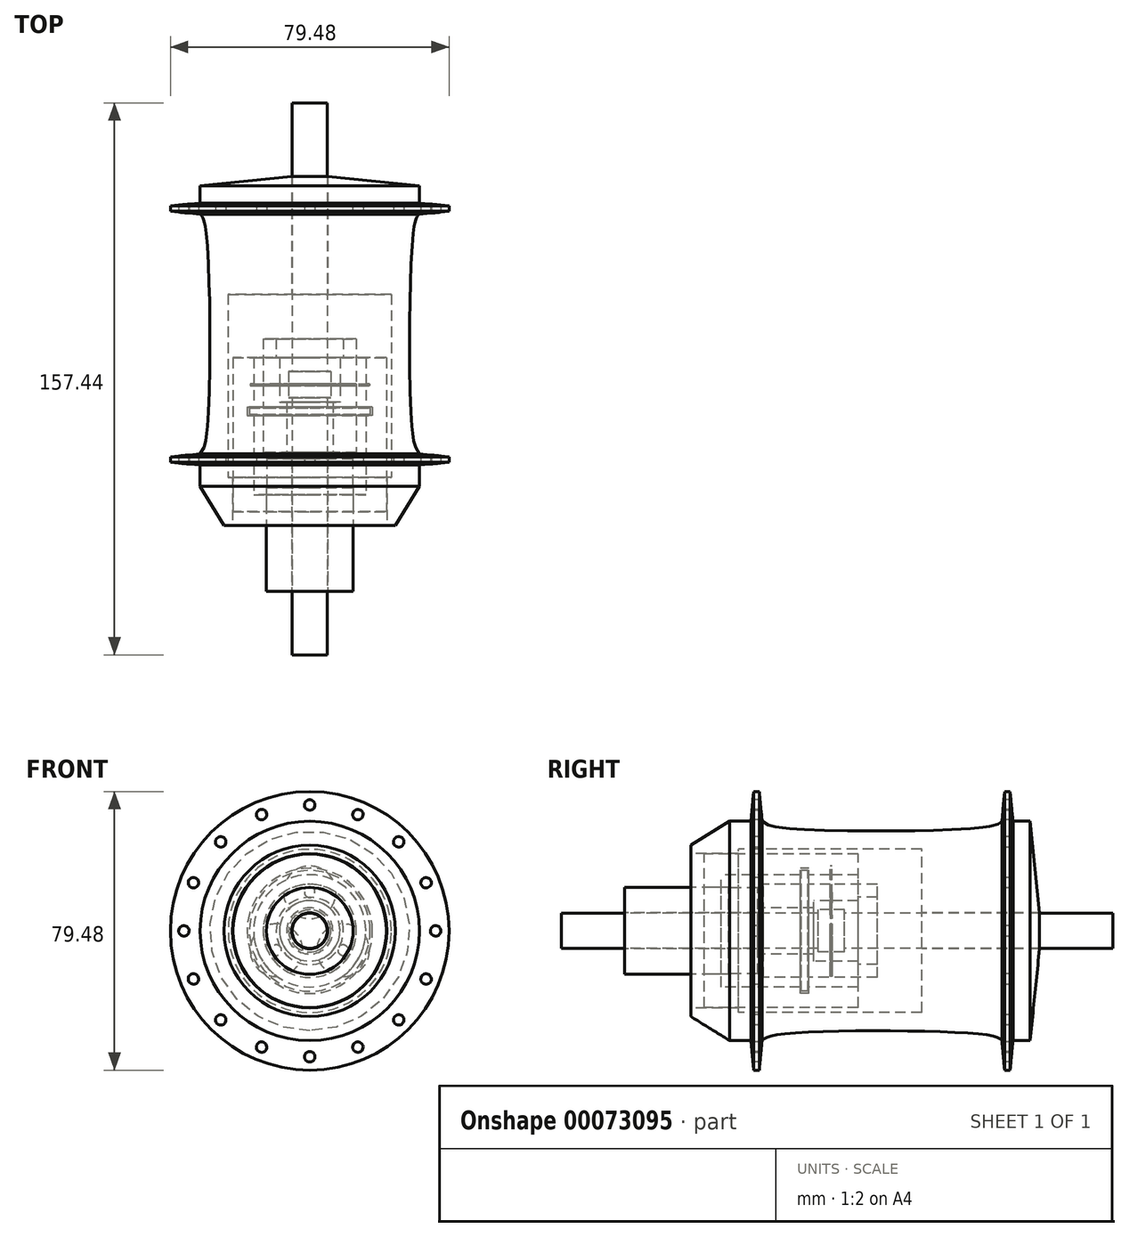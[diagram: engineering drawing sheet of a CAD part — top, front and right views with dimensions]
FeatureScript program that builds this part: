
annotation { "Feature Type Name" : "Feature", "Feature Type Description" : "" }
export const myFeature = defineFeature(function(context is Context, id is Id, definition is map)
    precondition{}
    {
        {
            assignVariable(context, id + "F0", {"name" : "gearWidth", "anyValue" : .5});
        }
        {
            var Q0;
            Q0=qCreatedBy(makeId("Right.planeOp"),FACE);
            var sketch = newSketch(context, id + "F1", { "sketchPlane" : qUnion([Q0])});
            skLineSegment(sketch, "E0", {"start": v(-26.68, 31.27) * mm, "end": v(-20.6, 31.27) * mm});
            skLineSegment(sketch, "E1", {"start": v(59.06, 31.27) * mm, "end": v(61.75, 5.13) * mm});
            skLineSegment(sketch, "E2", {"start": v(61.75, 5.13) * mm, "end": v(28.14, 5.13) * mm});
            skLineSegment(sketch, "E3", {"start": v(28.14, 5.13) * mm, "end": v(28.14, 23.27) * mm});
            skLineSegment(sketch, "E4", {"start": v(28.14, 23.27) * mm, "end": v(-24.12, 23.27) * mm});
            skLineSegment(sketch, "E5", {"start": v(-37.77, 24.44) * mm, "end": v(-26.68, 31.27) * mm});
            skLineSegment(sketch, "E6", {"start": v(-20.6, 31.27) * mm, "end": v(-19.8, 39.74) * mm});
            skLineSegment(sketch, "E7", {"start": v(-19.8, 39.74) * mm, "end": v(-18.22, 39.74) * mm});
            skLineSegment(sketch, "E8", {"start": v(-18.22, 39.74) * mm, "end": v(-17.43, 31.27) * mm});
            skLineSegment(sketch, "E9", {"start": v(50.99, 31.27) * mm, "end": v(51.78, 39.74) * mm});
            skLineSegment(sketch, "E10", {"start": v(51.78, 39.74) * mm, "end": v(53.37, 39.74) * mm});
            skLineSegment(sketch, "E11", {"start": v(53.37, 39.74) * mm, "end": v(54.16, 31.27) * mm});
            skLineSegment(sketch, "E12.trimOffspring", {"start": v(54.16, 31.27) * mm, "end": v(59.06, 31.27) * mm});
            skLineSegment(sketch, "E13", {"start": v(-67.5, 0) * mm, "end": v(67.5, 0) * mm, "construction": true});
            skFitSpline(sketch, "E14", {"points": [v(-17.43, 31.27) * mm, v(-13, 29.59) * mm, v(46.1, 29.59) * mm, v(50.99, 31.27) * mm], "startDerivative": vector(15.28, -10.7) * mm, "endDerivative": vector(11.9, 12.75) * mm});
            skLineSegment(sketch, "E15", {"start": v(-33.92, 21.88) * mm, "end": v(10.01, 21.88) * mm});
            skLineSegment(sketch, "E16.bottom", {"start": v(-74.74, 5) * mm, "end": v(-1.42, 5) * mm});
            skLineSegment(sketch, "E16.top", {"start": v(-74.74, 0) * mm, "end": v(82.7, 0) * mm});
            skLineSegment(sketch, "E16.left", {"start": v(-74.74, 5) * mm, "end": v(-74.74, 0) * mm});
            skLineSegment(sketch, "E16.right", {"start": v(82.7, 5) * mm, "end": v(82.7, 0) * mm});
            skLineSegment(sketch, "E17.bottom", {"start": v(-56.63, 12.38) * mm, "end": v(-26.97, 12.38) * mm});
            skLineSegment(sketch, "E17.top", {"start": v(-56.63, 5.13) * mm, "end": v(-18.73, 5.13) * mm});
            skLineSegment(sketch, "E17.left", {"start": v(-56.63, 12.38) * mm, "end": v(-56.63, 5.13) * mm});
            skLineSegment(sketch, "E17.right", {"start": v(-18.73, 12.38) * mm, "end": v(-18.73, 5.13) * mm});
            skLineSegment(sketch, "E18.top", {"start": v(-18.73, 12.27) * mm, "end": v(-26.97, 12.27) * mm});
            skLineSegment(sketch, "E18.left", {"start": v(-18.73, 12.27) * mm, "end": v(-18.73, 12.38) * mm});
            skLineSegment(sketch, "E18.right", {"start": v(-26.97, 12.27) * mm, "end": v(-26.97, 12.38) * mm});
            skLineSegment(sketch, "E19", {"start": v(-33.92, 21.88) * mm, "end": v(-33.92, 16) * mm});
            skLineSegment(sketch, "E20", {"start": v(-29.03, 16) * mm, "end": v(-6.49, 16) * mm});
            skLineSegment(sketch, "E21", {"start": v(10.01, 16) * mm, "end": v(10.01, 21.88) * mm});
            skLineSegment(sketch, "E22.top", {"start": v(-37.77, 22.01) * mm, "end": v(-24.12, 22.01) * mm});
            skLineSegment(sketch, "E22.left", {"start": v(-37.77, 24.44) * mm, "end": v(-37.77, 22.01) * mm});
            skLineSegment(sketch, "E22.right", {"start": v(-24.12, 23.27) * mm, "end": v(-24.12, 22.01) * mm});
            skLineSegment(sketch, "E23.top", {"start": v(-33.92, 12.4) * mm, "end": v(-29.03, 12.4) * mm});
            skLineSegment(sketch, "E23.left", {"start": v(-33.92, 16) * mm, "end": v(-33.92, 12.4) * mm});
            skLineSegment(sketch, "E23.right", {"start": v(-29.03, 16) * mm, "end": v(-29.03, 12.4) * mm});
            skLineSegment(sketch, "E24.bottom", {"start": v(-17.02, 13.28) * mm, "end": v(-6.23, 13.28) * mm});
            skLineSegment(sketch, "E24.top", {"start": v(-17.02, 6.6) * mm, "end": v(-2.69, 6.6) * mm});
            skLineSegment(sketch, "E24.left", {"start": v(-17.02, 13.28) * mm, "end": v(-17.02, 6.6) * mm});
            skLineSegment(sketch, "E24.right", {"start": v(-2.69, 8.63) * mm, "end": v(-2.69, 6.6) * mm});
            skLineSegment(sketch, "E25.left", {"start": v(-6.49, 16) * mm, "end": v(-6.49, 17.88) * mm});
            skLineSegment(sketch, "E25.right", {"start": v(-4.03, 16) * mm, "end": v(-4.03, 17.88) * mm});
            skLineSegment(sketch, "E26.trimOffspring", {"start": v(-4.03, 16) * mm, "end": v(10.01, 16) * mm});
            skLineSegment(sketch, "E27", {"start": v(-4.03, 17.88) * mm, "end": v(-6.49, 17.88) * mm});
            skLineSegment(sketch, "E28.top", {"start": v(-6.23, 17.23) * mm, "end": v(-4.29, 17.23) * mm});
            skLineSegment(sketch, "E28.left", {"start": v(-6.23, 13.28) * mm, "end": v(-6.23, 17.23) * mm});
            skLineSegment(sketch, "E28.right", {"start": v(-4.29, 13.28) * mm, "end": v(-4.29, 17.23) * mm});
            skLineSegment(sketch, "E29.trimOffspring", {"start": v(-4.29, 13.28) * mm, "end": v(-2.69, 13.28) * mm});
            skPoint(sketch, "E30", {"position": v(-5.26, 17.23) * mm});
            skPoint(sketch, "E31", {"position": v(-5.26, 17.88) * mm});
            skLineSegment(sketch, "E32.top", {"start": v(-1.42, 6) * mm, "end": v(6.08, 6) * mm});
            skLineSegment(sketch, "E32.left", {"start": v(-1.42, 5) * mm, "end": v(-1.42, 6) * mm});
            skLineSegment(sketch, "E32.right", {"start": v(6.08, 5) * mm, "end": v(6.08, 6) * mm});
            skLineSegment(sketch, "E33.trimOffspring", {"start": v(6.08, 5) * mm, "end": v(82.7, 5) * mm});
            skLineSegment(sketch, "E34.bottom", {"start": v(-2.69, 13.28) * mm, "end": v(10.01, 13.28) * mm});
            skLineSegment(sketch, "E34.top", {"start": v(-2.69, 8.63) * mm, "end": v(10.01, 8.63) * mm});
            skLineSegment(sketch, "E35.bottom", {"start": v(10.01, 13.28) * mm, "end": v(15.44, 13.28) * mm});
            skLineSegment(sketch, "E35.top", {"start": v(10.01, 9.58) * mm, "end": v(15.44, 9.58) * mm});
            skLineSegment(sketch, "E35.left", {"start": v(10.01, 9.58) * mm, "end": v(10.01, 8.63) * mm});
            skLineSegment(sketch, "E35.right", {"start": v(15.44, 13.28) * mm, "end": v(15.44, 9.58) * mm});
            skPoint(sketch, "E36", {"position": v(-22.85, 12.27) * mm});
            skLineSegment(sketch, "E37", {"start": v(2.33, 6) * mm, "end": v(2.33, 16) * mm, "construction": true});
            skPoint(sketch, "E38", {"position": v(2.33, 11) * mm});
            skSolve(sketch);
        }
        {
            var Q0;
            Q0=makeQuery(id+"F1.imprint","IMPRINT",FACE,{"disambiguationData":[TD([[makeQuery(id+"F1.imprint","IMPRINT",EDGE,{"derivedFrom":sQuery(id+"F1.wireOp",EDGE,"E0")}),-1.0]])]});
            var Q1;
            Q1=makeQuery(id+"F1.imprint","IMPRINT",FACE,{"disambiguationData":[TD([[makeQuery(id+"F1.imprint","IMPRINT",EDGE,{"derivedFrom":sQuery(id+"F1.wireOp",EDGE,"E15")}),-1.0]])]});
            var Q2;
            Q2=makeQuery(id+"F1.imprint","IMPRINT",FACE,{"disambiguationData":[TD([[makeQuery(id+"F1.imprint","IMPRINT",EDGE,{"derivedFrom":sQuery(id+"F1.wireOp",EDGE,"E17.bottom")}),-1.0]])]});
            var Q3;
            Q3=makeQuery(id+"F1.imprint","IMPRINT",FACE,{"disambiguationData":[TD([[makeQuery(id+"F1.imprint","IMPRINT",EDGE,{"derivedFrom":sQuery(id+"F1.wireOp",EDGE,"E16.bottom")}),-1.0]])]});
            var Q4;
            Q4=makeQuery(id+"F1.imprint","IMPRINT",FACE,{"disambiguationData":[TD([[makeQuery(id+"F1.imprint","IMPRINT",EDGE,{"derivedFrom":sQuery(id+"F1.wireOp",EDGE,"E24.bottom")}),-1.0]])]});
            var Q5;
            Q5=sQuery(id+"F1.wireOp",EDGE,"E13");
            revolve(context, id + "F2", {"entities" : qUnion([Q0, Q1, Q2, Q3, Q4]), "axis" : qUnion([Q5]), "revolveType" : RevolveType.FULL});
        }
        {
            var Q0;
            Q0=qCreatedBy(makeId("Front.planeOp"),FACE);
            var Q1;
            Q1=sQuery(id+"F1.wireOp",VERTEX,"E38");
            cPlane(context, id + "F3", {"entities" : qUnion([Q0, Q1]), "cplaneType" : CPlaneType.PLANE_POINT, "offset" : 152.4 * mm, "width" : 152.4 * mm, "height" : 152.4 * mm});
        }
        {
            var Q0;
            Q0=qCreatedBy(id+"F3.planeOp",FACE);
            var sketch = newSketch(context, id + "F4", { "sketchPlane" : qUnion([Q0])});
            skCircle(sketch, "E39", {"center": v(0, 11) * mm, "radius": 1.5 * mm});
            skCircle(sketch, "E40", {"center": v(0, 11) * mm, "radius": 7.5 * mm});
            skCircle(sketch, "E41.1.0", {"center": v(-9.53, -5.5) * mm, "radius": 7.5 * mm});
            skCircle(sketch, "E41.1.1", {"center": v(-9.53, -5.5) * mm, "radius": 1.5 * mm});
            skCircle(sketch, "E41.2.0", {"center": v(9.53, -5.5) * mm, "radius": 7.5 * mm});
            skCircle(sketch, "E41.2.1", {"center": v(9.53, -5.5) * mm, "radius": 1.5 * mm});
            skPoint(sketch, "E41.center", {"position": v(0, 0) * mm});
            skSolve(sketch);
        }
        {
            var Q0;
            Q0 = qSketchRegion(id + "F4", true);
            extrude(context, id + "F5", {"entities" : qUnion([Q0]), "operationType" : NewBodyOperationType.REMOVE, "oppositeDirection" : true, "depth" : (getVariable(context, 'gearWidth') * 1) * mm, "symmetric" : true});
        }
        {
            var Q0;
            Q0=qCreatedBy(makeId("Front.planeOp"),FACE);
            var sketch = newSketch(context, id + "F6", { "sketchPlane" : qUnion([Q0])});
            skCircle(sketch, "E42", {"center": v(0, 35.91) * mm, "radius": 1.5 * mm});
            skCircle(sketch, "E43.1.0", {"center": v(-13.74, 33.18) * mm, "radius": 1.5 * mm});
            skCircle(sketch, "E43.2.0", {"center": v(-25.4, 25.4) * mm, "radius": 1.5 * mm});
            skCircle(sketch, "E43.3.0", {"center": v(-33.18, 13.74) * mm, "radius": 1.5 * mm});
            skCircle(sketch, "E43.4.0", {"center": v(-35.91, 0) * mm, "radius": 1.5 * mm});
            skCircle(sketch, "E43.5.0", {"center": v(-33.18, -13.74) * mm, "radius": 1.5 * mm});
            skCircle(sketch, "E43.6.0", {"center": v(-25.4, -25.4) * mm, "radius": 1.5 * mm});
            skCircle(sketch, "E43.7.0", {"center": v(-13.74, -33.18) * mm, "radius": 1.5 * mm});
            skCircle(sketch, "E43.8.0", {"center": v(0, -35.91) * mm, "radius": 1.5 * mm});
            skCircle(sketch, "E43.9.0", {"center": v(13.74, -33.18) * mm, "radius": 1.5 * mm});
            skCircle(sketch, "E43.10.0", {"center": v(25.4, -25.4) * mm, "radius": 1.5 * mm});
            skCircle(sketch, "E43.11.0", {"center": v(33.18, -13.74) * mm, "radius": 1.5 * mm});
            skCircle(sketch, "E43.12.0", {"center": v(35.91, 0) * mm, "radius": 1.5 * mm});
            skCircle(sketch, "E43.13.0", {"center": v(33.18, 13.74) * mm, "radius": 1.5 * mm});
            skCircle(sketch, "E43.14.0", {"center": v(25.4, 25.4) * mm, "radius": 1.5 * mm});
            skCircle(sketch, "E43.15.0", {"center": v(13.74, 33.18) * mm, "radius": 1.5 * mm});
            skPoint(sketch, "E43.center", {"position": v(0, 0) * mm});
            skSolve(sketch);
        }
        {
            var Q0;
            Q0 = qSketchRegion(id + "F6", true);
            extrude(context, id + "F7", {"entities" : qUnion([Q0]), "operationType" : NewBodyOperationType.REMOVE, "oppositeDirection" : true, "depth" : 127 * mm, "symmetric" : true});
        }
    });
